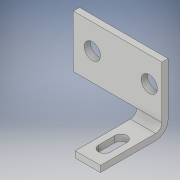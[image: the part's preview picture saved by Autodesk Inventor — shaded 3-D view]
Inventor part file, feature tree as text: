
AUTODESK INVENTOR PART (.ipt)
format: ipt  version: 2017 (Build 210142000, 142)  size: 181,248 bytes
history: native  units: in
note: dims shown in document units (in); Inventor stores cm internally (conversion verified against a paired STEP export)
features: sketch x5, extrude x4, other x1
ambient origin geometry x8: Origin, YZ Plane, XZ Plane, XY Plane, X Axis, Y Axis, Z Axis, Center Point
bodies: Solid1 (feature_tree)
feature tree (10):
  extrude  "Extrusion1"  Depth=0.496in
  extrude  "Extrusion2"  Depth=0.238in
  extrude  "Extrusion4"  Depth=0.059in
  extrude  "Extrusion5"  Depth=0.238in
  other  "Bend Part2"
  sketch  "Sketch1"  dims[d0=0.838in d1=0.496in]
  sketch  "Sketch2"  dims[d2=0.238in d3=0.615in]
  sketch  "Sketch3"  dims[d4=0.059in d5=0.0in d6=0.154in]
  sketch  "Sketch6"  dims[d7=0.238in d8=0.18in]
  sketch  "Sketch16"  dims[d9=0.7874in d11=0.539in d12=0.3937in d14=1.0in d16=1.0in d17=0.0in d18=0.114in d19=0.157in d20=0.119in d24=0.7874in d26=0.156in d27=0.3937in d29=1.0in d31=1.0in d32=0.0in d33=1.0in d34=0.0in d51=0.059in d52=90.0deg]
